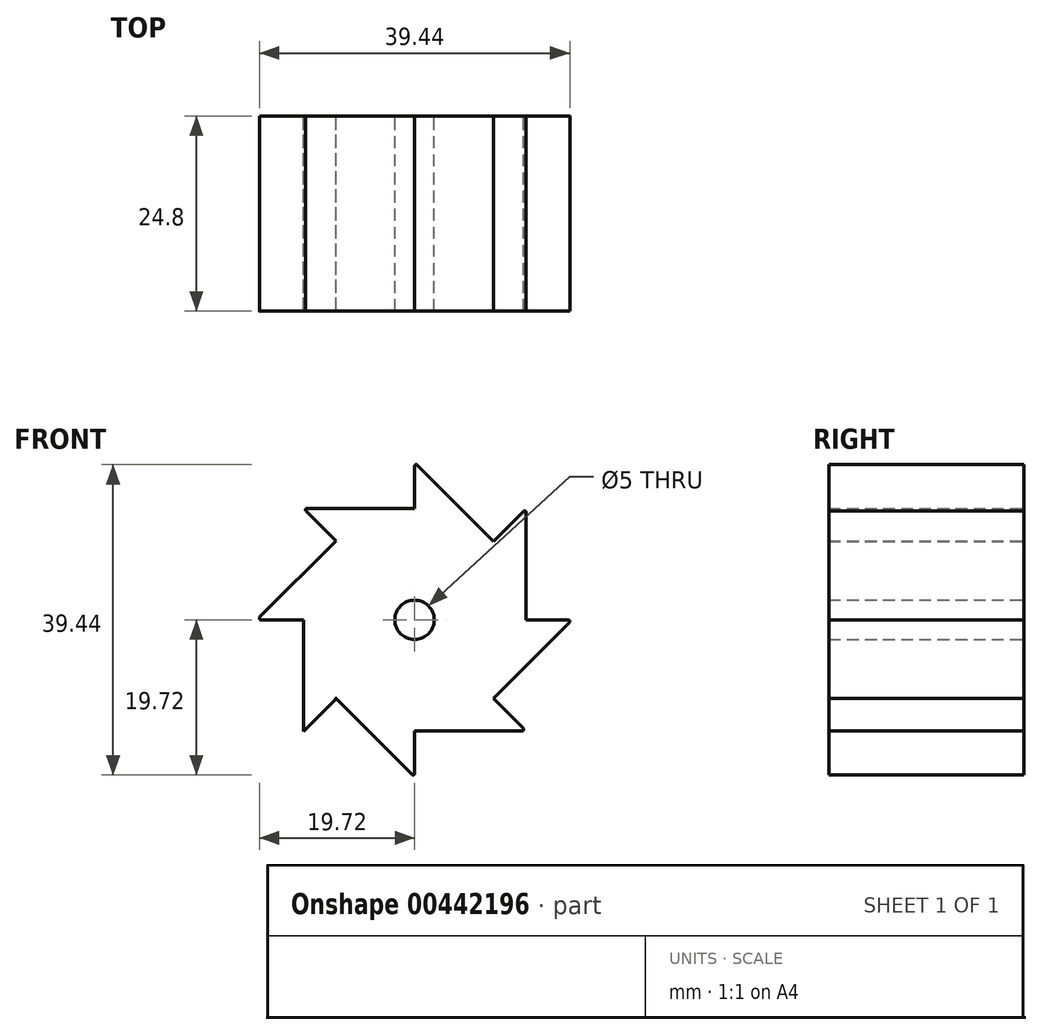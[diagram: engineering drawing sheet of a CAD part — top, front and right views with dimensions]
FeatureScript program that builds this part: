
annotation { "Feature Type Name" : "Feature", "Feature Type Description" : "" }
export const myFeature = defineFeature(function(context is Context, id is Id, definition is map)
    precondition{}
    {
        {
            var Q0;
            Q0=qCreatedBy(makeId("Front.planeOp"),FACE);
            var sketch = newSketch(context, id + "F0", { "sketchPlane" : qUnion([Q0])});
            skLineSegment(sketch, "E0", {"start": v(0, 20) * mm, "end": v(0, 14.15) * mm});
            skLineSegment(sketch, "E1", {"start": v(-20, 0) * mm, "end": v(-14.12, 0) * mm});
            skLineSegment(sketch, "E2", {"start": v(-14.13, 14.15) * mm, "end": v(-9.99, 10.01) * mm});
            skLineSegment(sketch, "E3", {"start": v(14.17, 14.12) * mm, "end": v(10.03, 9.97) * mm});
            skLineSegment(sketch, "E4", {"start": v(0, 20) * mm, "end": v(10.03, 9.97) * mm});
            skLineSegment(sketch, "E5", {"start": v(14.17, 14.12) * mm, "end": v(14.17, 0) * mm});
            skLineSegment(sketch, "E6", {"start": v(14.17, 0) * mm, "end": v(20, 0) * mm});
            skLineSegment(sketch, "E7", {"start": v(20, 0) * mm, "end": v(10.01, -9.99) * mm});
            skLineSegment(sketch, "E8", {"start": v(14.15, -14.13) * mm, "end": v(0, -14.13) * mm});
            skLineSegment(sketch, "E9", {"start": v(0, -20) * mm, "end": v(-9.97, -10.03) * mm});
            skLineSegment(sketch, "E10", {"start": v(-14.12, -14.17) * mm, "end": v(-14.12, 0) * mm});
            skLineSegment(sketch, "E11", {"start": v(-20, 0) * mm, "end": v(-9.99, 10.01) * mm});
            skLineSegment(sketch, "E12", {"start": v(-14.13, 14.15) * mm, "end": v(0, 14.15) * mm});
            skCircle(sketch, "E13", {"center": v(0, 0) * mm, "radius": 2.5 * mm});
            skLineSegment(sketch, "E14.trimOffspring", {"start": v(0.05, 0) * mm, "end": v(0, -0.05) * mm});
            skLineSegment(sketch, "E15.trimOffspring", {"start": v(10.01, -9.99) * mm, "end": v(14.15, -14.13) * mm});
            skLineSegment(sketch, "E16.trimOffspring", {"start": v(0, -14.13) * mm, "end": v(0, -20) * mm});
            skLineSegment(sketch, "E17.trimOffspring", {"start": v(0, 0.02) * mm, "end": v(0, -2.5) * mm});
            skLineSegment(sketch, "E18.trimOffspring", {"start": v(-9.97, -10.03) * mm, "end": v(-14.12, -14.17) * mm});
            skLineSegment(sketch, "E19.trimOffspring", {"start": v(0, 0) * mm, "end": v(0.05, 0) * mm});
            skLineSegment(sketch, "E20.trimOffspring", {"start": v(0, 0.02) * mm, "end": v(0.04, -0.02) * mm});
            skSolve(sketch);
        }
        {
            var Q0;
            Q0=makeQuery(id+"F0.imprint","IMPRINT",FACE,{"disambiguationData":[TD([[makeQuery(id+"F0.imprint","IMPRINT",EDGE,{"derivedFrom":sQuery(id+"F0.wireOp",EDGE,"E0")}),1.0]])]});
            extrude(context, id + "F1", {"entities" : qUnion([Q0]), "depth" : 24.8 * mm});
        }
        {
            var Q0;
            Q0=makeQuery(id+"F1.opExtrude","SWEPT_EDGE",EDGE,{"disambiguationData":[OSD([sQuery(id+"F0.wireOp",EDGE,"E0"),sQuery(id+"F0.wireOp",EDGE,"E4")])]});
            var Q1;
            Q1=makeQuery(id+"F1.opExtrude","SWEPT_EDGE",EDGE,{"disambiguationData":[OSD([sQuery(id+"F0.wireOp",EDGE,"E3"),sQuery(id+"F0.wireOp",EDGE,"E5")])]});
            var Q2;
            Q2=makeQuery(id+"F1.opExtrude","SWEPT_EDGE",EDGE,{"disambiguationData":[OSD([sQuery(id+"F0.wireOp",EDGE,"E7"),sQuery(id+"F0.wireOp",EDGE,"E6")])]});
            var Q3;
            Q3=makeQuery(id+"F1.opExtrude","SWEPT_EDGE",EDGE,{"disambiguationData":[OSD([sQuery(id+"F0.wireOp",EDGE,"E8"),sQuery(id+"F0.wireOp",EDGE,"E15.trimOffspring")])]});
            var Q4;
            Q4=makeQuery(id+"F1.opExtrude","SWEPT_EDGE",EDGE,{"disambiguationData":[OSD([sQuery(id+"F0.wireOp",EDGE,"E9"),sQuery(id+"F0.wireOp",EDGE,"E16.trimOffspring")])]});
            var Q5;
            Q5=makeQuery(id+"F1.opExtrude","CAP_EDGE",EDGE,{"disambiguationData":[OSD([sQuery(id+"F0.wireOp",EDGE,"E18.trimOffspring")])],"isStart":false});
            var Q6;
            Q6=makeQuery(id+"F1.opExtrude","SWEPT_EDGE",EDGE,{"disambiguationData":[OSD([sQuery(id+"F0.wireOp",EDGE,"E1"),sQuery(id+"F0.wireOp",EDGE,"E11")])]});
            var Q7;
            Q7=makeQuery(id+"F1.opExtrude","SWEPT_EDGE",EDGE,{"disambiguationData":[OSD([sQuery(id+"F0.wireOp",EDGE,"E2"),sQuery(id+"F0.wireOp",EDGE,"E12")])]});
            fillet(context, id + "F2", {"entities" : qUnion([Q0, Q1, Q2, Q3, Q4, Q5, Q6, Q7]), "radius" : 0.2 * mm, "tangentPropagation" : true, "allowEdgeOverflow" : false});
        }
    });
